# Revit family: PFX_A3-Toilet-Cubicle-Ed-Adjacent-Wall
name_source: partatom
category: Generic Models
revit_build: Autodesk Revit 2016 (Build: 20150220_1215(x64)
units: mm (PartAtom-declared; Revit-internal decimal feet)

## family parameters
Always vertical = Yes
Can host rebar = No
Cut with Voids When Loaded = No
Part Type = Undefined
Room Calculation Point = No
Round Connector Dimension = Use Diameter
Shared = No
Work Plane-Based = No

## types (1)
- ED Adjacent Wall
    Base Offset = 150 mm
    Bttm Frame Depth = 45 mm  [stored 0.147638 ft]
    Cubicle Clear Width = 800 mm  [stored 2.62467 ft]
    Cubicle Depth = 1500 mm  [stored 4.92126 ft]
    Cubicle Height = 1800 mm  [stored 5.90551 ft]
    Cubicle Panel Thickness = 20 mm  [stored 0.0656168 ft]
    Cubicle Width = 820 mm
    Door Head Clearance = 10 mm  [stored 0.0328084 ft]
    Door Width = 755 mm
    Handle Mounting Height = 800 mm  [stored 2.62467 ft]
    Keynote = K32
    Material Cubicle Feet = Toilet Cubicle Feet
    Material Cubicle Frame = Toilet Cubicle Frame
    Material Cubicle Panels = Toilet Cubicle Panelling
    Plumbing Duct Depth = 300 mm
    Top Frame Depth = 45 mm  [stored 0.147638 ft]
    Vis - Cubicle Legs = Yes
    Vis - Door LHS = Yes
    Vis - Door RHS = No
    Vis - Placement Lines = Yes

note: [stored X ft] marks values corroborated as IEEE doubles in the binary element streams (Revit-internal decimal feet)

## geometry (parser evidence)
native form markers: Sweep x7
no freeform markers — native parametric forms only
